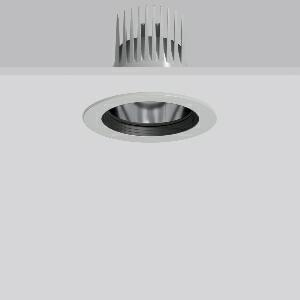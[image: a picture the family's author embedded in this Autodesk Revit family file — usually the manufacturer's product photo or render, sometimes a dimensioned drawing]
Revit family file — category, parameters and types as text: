
# Revit family: heledon_maxi_e_901757_004_1_c067
name_source: partatom
category: Lighting Fixtures
units: mm (PartAtom-declared; Revit-internal decimal feet)

## family parameters
Cut with Voids When Loaded = No
Host = Face
Light Source = No
Part Type = Normal
Room Calculation Point = No
Round Connector Dimension = Use Diameter
Shared = No

## types (1)
- HELEDON maxi E (1 x LED Modul 940, 3500 lm, 4000)
    Apparent Load = 25 VA
    Approval mark = CE
    CIE Flux Codes = 100 100 100 100 100
    Color Rendering = 92
    Color Temperature = 4000
    Default Elevation = 1800 mm
    Description = Series: HELEDON maxi
Round recessed downlight. Housing: die-cast aluminium, powder-coated. Black plastic ring and recessed LED to prevent glare from the side. Optical assembly with reflector made of MIRO-Silver with 98% total light reflection for outstanding efficiency - can be changed without tools. Best colour rendering index Ra>90. Suitable for Recessed ceiling mounting. Installation without tools thanks to spring fastening system. Including separate LED converter with connecting cable 600 mm.High quality converter without flickering and stroboscopic effect. Through-wiring box (5 pole) available as accessory. The following accessories can be mounted without use of tools: interchangeable lenses, decorative glasses, honeycomb louvre, clear and frosted diffusers, white interchangeable plastic ring. 
Colour: silver
Diameter: 162 mm
Height: 3 mm
Cut-out diameter: 152 mm
Recess height: 200 mm
Luminaire: recess height: 135 mm
Lamp: LED
Socket: without socket
Colour temperature: 4000K
Colour rendering index (CRI): 92
System power: 25 W
Rated luminous flux: 3500 lm
Luminous efficiency: 140 lm/W
Control gear: Regulated power supply
Protection class: II
Type of protection: IP 20
    Height = 0 mm  [stored 0 ft]
    Lamp = 1 x LED Modul 940
    Lamp Light Flux = 3500 lm
    Lamp count = 1
    Length = 162 mm
    Lifetime = 50000 h
    Luminous efficacy = 140 lm/W
    Manufacturer = RZB
    ModVariant = No
    Model = 901757.004.1
    Mounting Place = Ceiling
    Mounting Type = Recessed
    Number of Poles = 1
    OnlyDefault = Yes
    Power Factor = 1
    Product Name = HELEDON maxi E
    Product group = Recessed downlights
    ProductGroupID = 402
    Protection Class = Protection class II
    Protection Degree = IP 20
    RLX_Detail_Level = 1
    RLX_Emergency_Light_Flux = 0 lm
    RLX_Emergency_Type = 0
    RLX_Emergency_Type_DB = No
    RlxData = <blob elided: 119089 chars, md5=15d6186d>
    Socket = socket
    Standby Power = 0 W
    System Light Flux = 3500 lm
    System Power = 25 W
    Type Comments = Product without accessories
    Type Image = 901662.004.jpg
    URL = http://relux.com
    VarID = ---
    Voltage = 230 V
    Voltage Range = 220-240 V
    Weight = 0.00 kg
    Width = 0 mm  [stored 0 ft]

note: [stored X ft] marks values corroborated as IEEE doubles in the binary element streams (Revit-internal decimal feet)

## geometry (parser evidence)
native form markers: Blend x4, Sweep x11
no freeform markers — native parametric forms only
